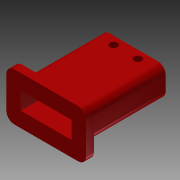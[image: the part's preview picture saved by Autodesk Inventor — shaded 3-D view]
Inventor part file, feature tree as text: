
AUTODESK INVENTOR PART (.ipt)
format: ipt  version: 2015 (Build 190159000, 159)  size: 134,144 bytes
history: native  units: in
note: dims shown in document units (in); Inventor stores cm internally (conversion verified against a paired STEP export)
features: extrude x3, sketch x3, shell x1, fillet x1
ambient origin geometry x8: Origin, YZ Plane, XZ Plane, XY Plane, X Axis, Y Axis, Z Axis, Center Point
bodies: Solid1 (feature_tree)
feature tree (8):
  extrude  "Extrusion1"  Depth=0.474in
  shell  "Shell1"  Thickness=1.25in
  extrude  "Extrusion2"  Depth=0.125in
  extrude  "Extrusion3"  Depth=0.125in
  fillet  "Fillet1"  Radius=0.5in
  sketch  "Sketch1"  dims[d0=1.0in d1=0.474in d2=1.25in d3=0.0in]
  sketch  "Sketch2"  dims[d4=0.1in d23=0.125in]
  sketch  "Sketch3"  dims[d24=0.12in d25=0.38in d26=0.5in d27=0.0in d28=0.75in d29=1.25in d30=0.125in d31=0.125in d32=0.0in d33=0.125in]
